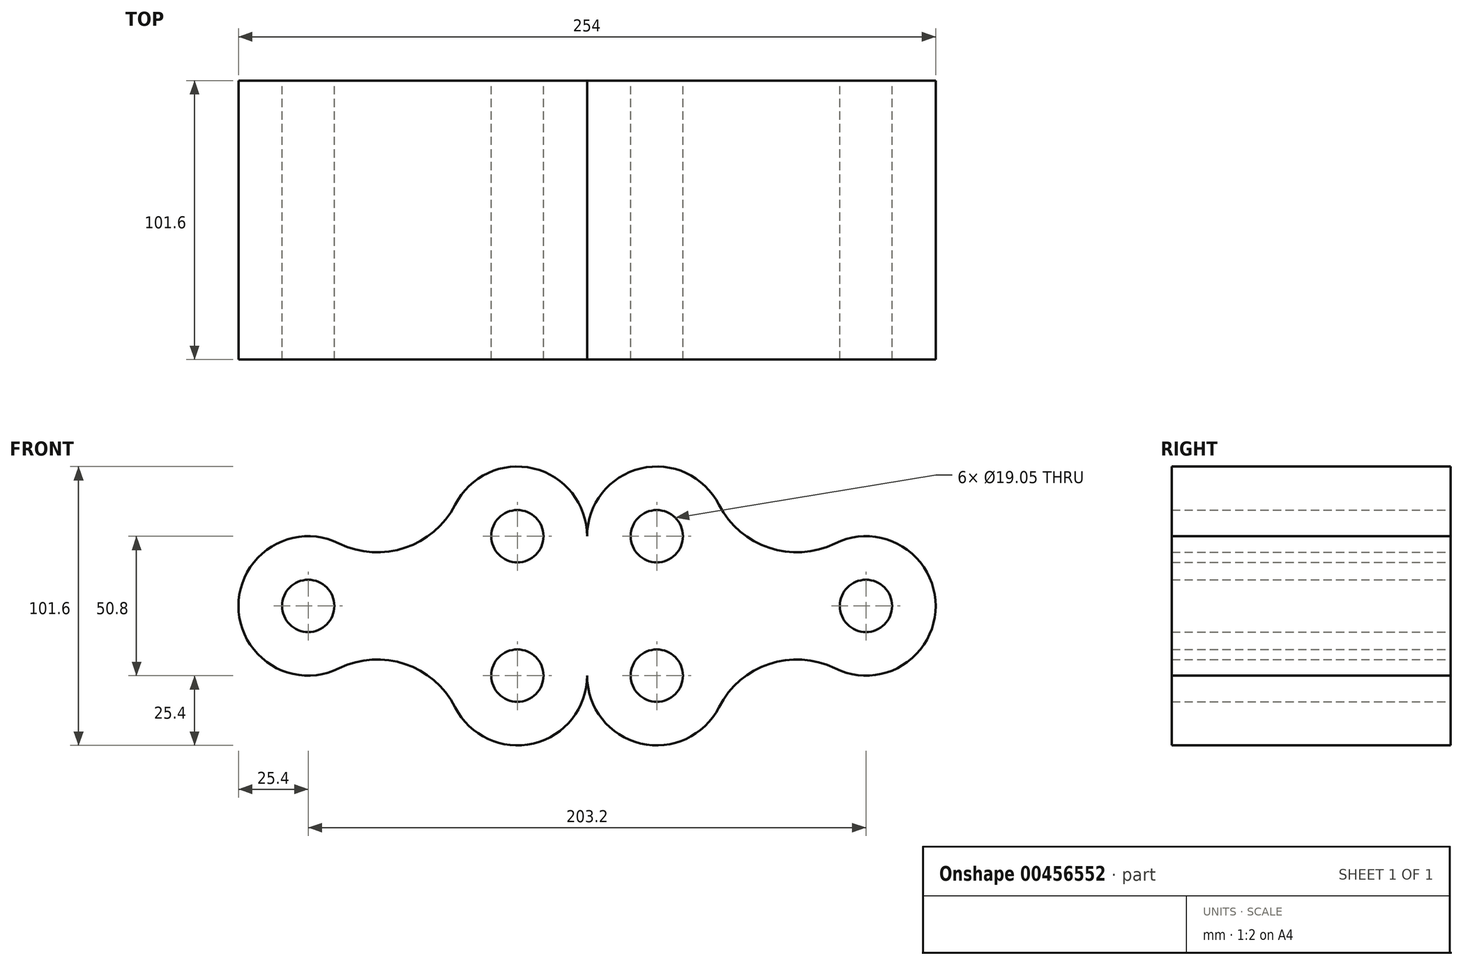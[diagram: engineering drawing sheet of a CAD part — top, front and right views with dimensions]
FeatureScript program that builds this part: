
annotation { "Feature Type Name" : "Feature", "Feature Type Description" : "" }
export const myFeature = defineFeature(function(context is Context, id is Id, definition is map)
    precondition{}
    {
        {
            var Q0;
            Q0=qCreatedBy(makeId("Front.planeOp"),FACE);
            var sketch = newSketch(context, id + "F0", { "sketchPlane" : qUnion([Q0])});
            skCircle(sketch, "E0", {"center": v(0, 0) * mm, "radius": 25.4 * mm});
            skCircle(sketch, "E1", {"center": v(0, 0) * mm, "radius": 9.53 * mm});
            skArc(sketch, "E2", {"start": v(101.6, 25.4) * mm, "mid": v(82.1, 50.1) * mm, "end": v(53.54, 36.88) * mm});
            skCircle(sketch, "E3", {"center": v(76.2, 25.4) * mm, "radius": 9.53 * mm});
            skArc(sketch, "E4.MirrorC", {"start": v(25.4, 0) * mm, "mid": v(-21.57, 13.4) * mm, "end": v(11.24, -22.78) * mm});
            skCircle(sketch, "E5", {"center": v(25.27, 51.2) * mm, "radius": 31.7 * mm, "construction": true});
            skArc(sketch, "E6", {"start": v(11.24, 22.78) * mm, "mid": v(35.28, 21.17) * mm, "end": v(53.54, 36.88) * mm});
            skCircle(sketch, "E7.MirrorC", {"center": v(25.27, -51.2) * mm, "radius": 31.7 * mm, "construction": true});
            skArc(sketch, "E8.MirrorC", {"start": v(101.6, -25.4) * mm, "mid": v(82.1, -50.1) * mm, "end": v(53.54, -36.88) * mm});
            skCircle(sketch, "E9.MirrorC", {"center": v(76.2, -25.4) * mm, "radius": 9.53 * mm});
            skArc(sketch, "E10.MirrorC", {"start": v(11.24, -22.78) * mm, "mid": v(-25.4, 0) * mm, "end": v(11.24, 22.78) * mm});
            skArc(sketch, "E11.MirrorCS", {"start": v(11.24, -22.78) * mm, "mid": v(35.28, -21.17) * mm, "end": v(53.54, -36.88) * mm});
            skArc(sketch, "E12.MirrorC", {"start": v(101.6, 25.4) * mm, "mid": v(121.1, 50.1) * mm, "end": v(149.66, 36.88) * mm});
            skArc(sketch, "E13.MirrorC", {"start": v(101.6, -25.4) * mm, "mid": v(121.1, -50.1) * mm, "end": v(149.66, -36.88) * mm});
            skCircle(sketch, "E14.MirrorC", {"center": v(177.93, 51.2) * mm, "radius": 31.7 * mm, "construction": true});
            skCircle(sketch, "E15.MirrorC", {"center": v(203.2, 0) * mm, "radius": 9.53 * mm});
            skArc(sketch, "E16.MirrorCS", {"start": v(191.96, -22.78) * mm, "mid": v(167.92, -21.17) * mm, "end": v(149.66, -36.88) * mm});
            skArc(sketch, "E17.MirrorCS", {"start": v(191.96, 22.78) * mm, "mid": v(167.92, 21.17) * mm, "end": v(149.66, 36.88) * mm});
            skCircle(sketch, "E18.MirrorC", {"center": v(203.2, 0) * mm, "radius": 25.4 * mm});
            skCircle(sketch, "E19.MirrorC", {"center": v(177.93, -51.2) * mm, "radius": 31.7 * mm, "construction": true});
            skCircle(sketch, "E20.MirrorC", {"center": v(127, 25.4) * mm, "radius": 9.53 * mm});
            skCircle(sketch, "E21.MirrorC", {"center": v(127, -25.4) * mm, "radius": 9.53 * mm});
            skSolve(sketch);
        }
        {
            var Q0;
            Q0 = qSketchRegion(id + "F0", true);
            extrude(context, id + "F1", {"entities" : qUnion([Q0]), "endBound" : BoundingType.SYMMETRIC, "depth" : 101.6 * mm});
        }
    });
